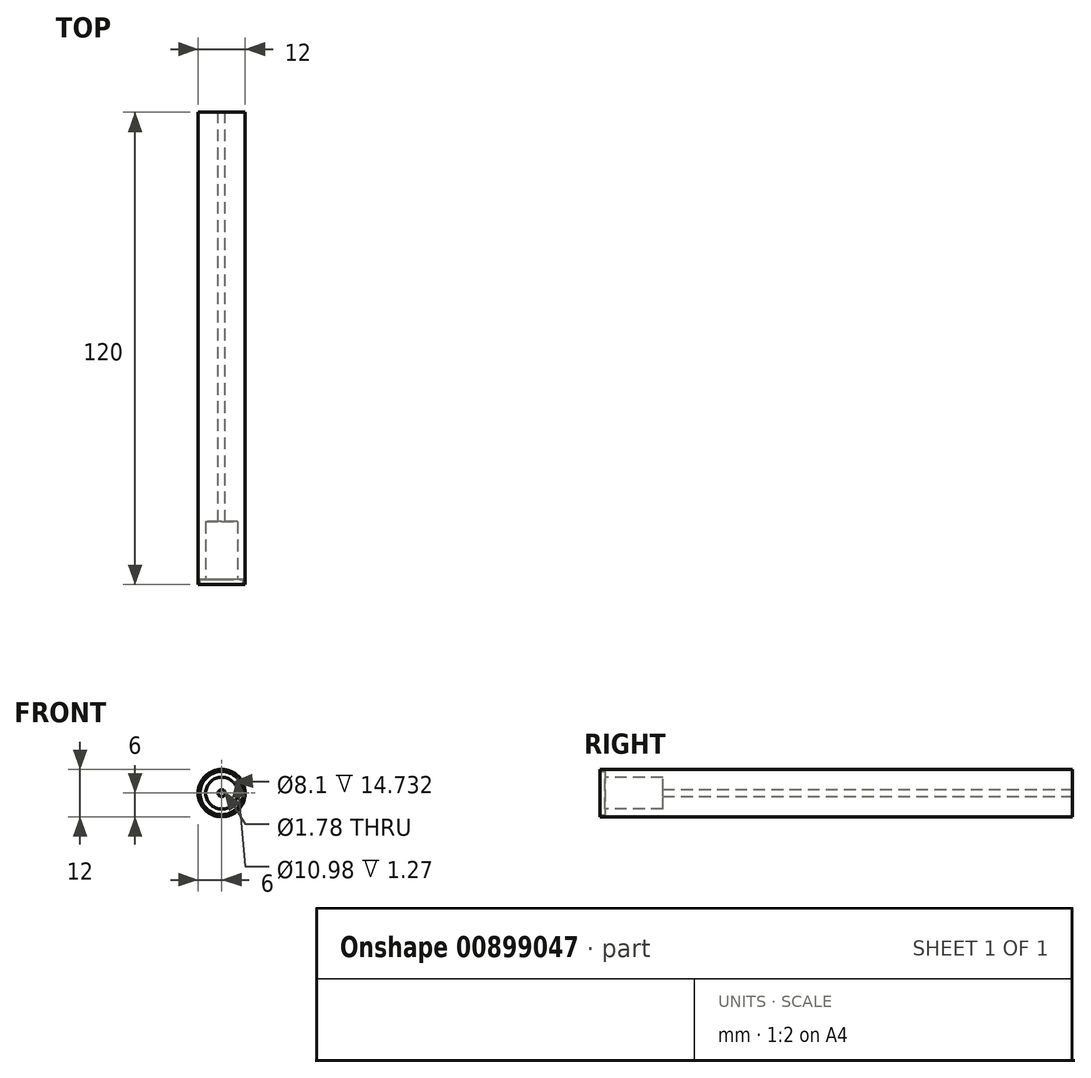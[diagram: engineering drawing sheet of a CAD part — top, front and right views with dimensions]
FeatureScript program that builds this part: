
annotation { "Feature Type Name" : "Feature", "Feature Type Description" : "" }
export const myFeature = defineFeature(function(context is Context, id is Id, definition is map)
    precondition{}
    {
        {
            var Q0;
            Q0=qCreatedBy(makeId("Front.planeOp"),FACE);
            var sketch = newSketch(context, id + "F0", { "sketchPlane" : qUnion([Q0])});
            skCircle(sketch, "E0", {"center": v(0, 0) * mm, "radius": 6 * mm});
            skSolve(sketch);
        }
        {
            var Q0;
            Q0 = qSketchRegion(id + "F0", true);
            extrude(context, id + "F1", {"entities" : qUnion([Q0]), "endBound" : BoundingType.SYMMETRIC, "depth" : 120 * mm, "offsetDistance" : 25.4 * mm});
        }
        {
            var Q0;
            Q0=makeQuery(id+"F1.opExtrude","CAP_FACE",FACE,{"disambiguationData":[OSD([sQuery(id+"F0.wireOp",EDGE,"E0")])],"isStart":false});
            var sketch = newSketch(context, id + "F2", { "sketchPlane" : qUnion([Q0])});
            skCircle(sketch, "E1.0.0", {"center": v(0, 0) * mm, "radius": 6 * mm});
            skCircle(sketch, "E2", {"center": v(0, 0) * mm, "radius": 4.05 * mm});
            skSolve(sketch);
        }
        {
            var Q0;
            Q0=makeQuery(id+"F2.imprint","IMPRINT",FACE,{"disambiguationData":[TD([[makeQuery(id+"F2.imprint","IMPRINT",EDGE,{"derivedFrom":sQuery(id+"F2.wireOp",EDGE,"E2")}),1.0]])]});
            extrude(context, id + "F3", {"entities" : qUnion([Q0]), "operationType" : NewBodyOperationType.REMOVE, "oppositeDirection" : true, "depth" : 16 * mm, "offsetDistance" : 25.4 * mm});
        }
        {
            var Q0;
            Q0=makeQuery(id+"F1.opExtrude","CAP_FACE",FACE,{"disambiguationData":[OSD([sQuery(id+"F0.wireOp",EDGE,"E0")])],"isStart":true});
            var sketch = newSketch(context, id + "F4", { "sketchPlane" : qUnion([Q0])});
            skCircle(sketch, "E3", {"center": v(0, 0) * mm, "radius": 0.89 * mm});
            skSolve(sketch);
        }
        {
            var Q0;
            Q0=makeQuery(id+"F4.imprint","IMPRINT",FACE,{"disambiguationData":[TD([[makeQuery(id+"F4.imprint","IMPRINT",EDGE,{"derivedFrom":sQuery(id+"F4.wireOp",EDGE,"E3")}),1.0]])]});
            extrude(context, id + "F5", {"entities" : qUnion([Q0]), "operationType" : NewBodyOperationType.REMOVE, "endBound" : BoundingType.THROUGH_ALL, "oppositeDirection" : true, "depth" : 25.4 * mm, "offsetDistance" : 25.4 * mm});
        }
        {
            var Q0;
            Q0=qCreatedBy(makeId("Top.planeOp"),FACE);
            var sketch = newSketch(context, id + "F6", { "sketchPlane" : qUnion([Q0])});
            skLineSegment(sketch, "E4.0.0", {"start": v(6, -60) * mm, "end": v(-6, -60) * mm});
            skLineSegment(sketch, "E5", {"start": v(-5.5, -60) * mm, "end": v(-5.5, -58.73) * mm});
            skLineSegment(sketch, "E6", {"start": v(-5.5, -58.73) * mm, "end": v(-3.84, -58.73) * mm});
            skLineSegment(sketch, "E7", {"start": v(-3.84, -58.73) * mm, "end": v(-3.84, -60) * mm});
            skLineSegment(sketch, "E8", {"start": v(0, -62.23) * mm, "end": v(0, -56.72) * mm, "construction": true});
            skSolve(sketch);
        }
        {
            var Q0;
            {var subQ0=sQuery(id+"F6.wireOp",EDGE,"E5");Q0=makeQuery(id+"F6.imprint","IMPRINT",FACE,{"disambiguationData":[TD([[makeQuery(id+"F6.imprint","IMPRINT",EDGE,{"derivedFrom":subQ0}),-1.0]])]});}
            var Q1;
            Q1=sQuery(id+"F6.wireOp",EDGE,"E8");
            revolve(context, id + "F7", {"operationType" : NewBodyOperationType.REMOVE, "surfaceOperationType" : NewSurfaceOperationType.NEW, "entities" : qUnion([Q0]), "axis" : qUnion([Q1]), "revolveType" : RevolveType.FULL, "oppositeDirection" : true});
        }
    });
